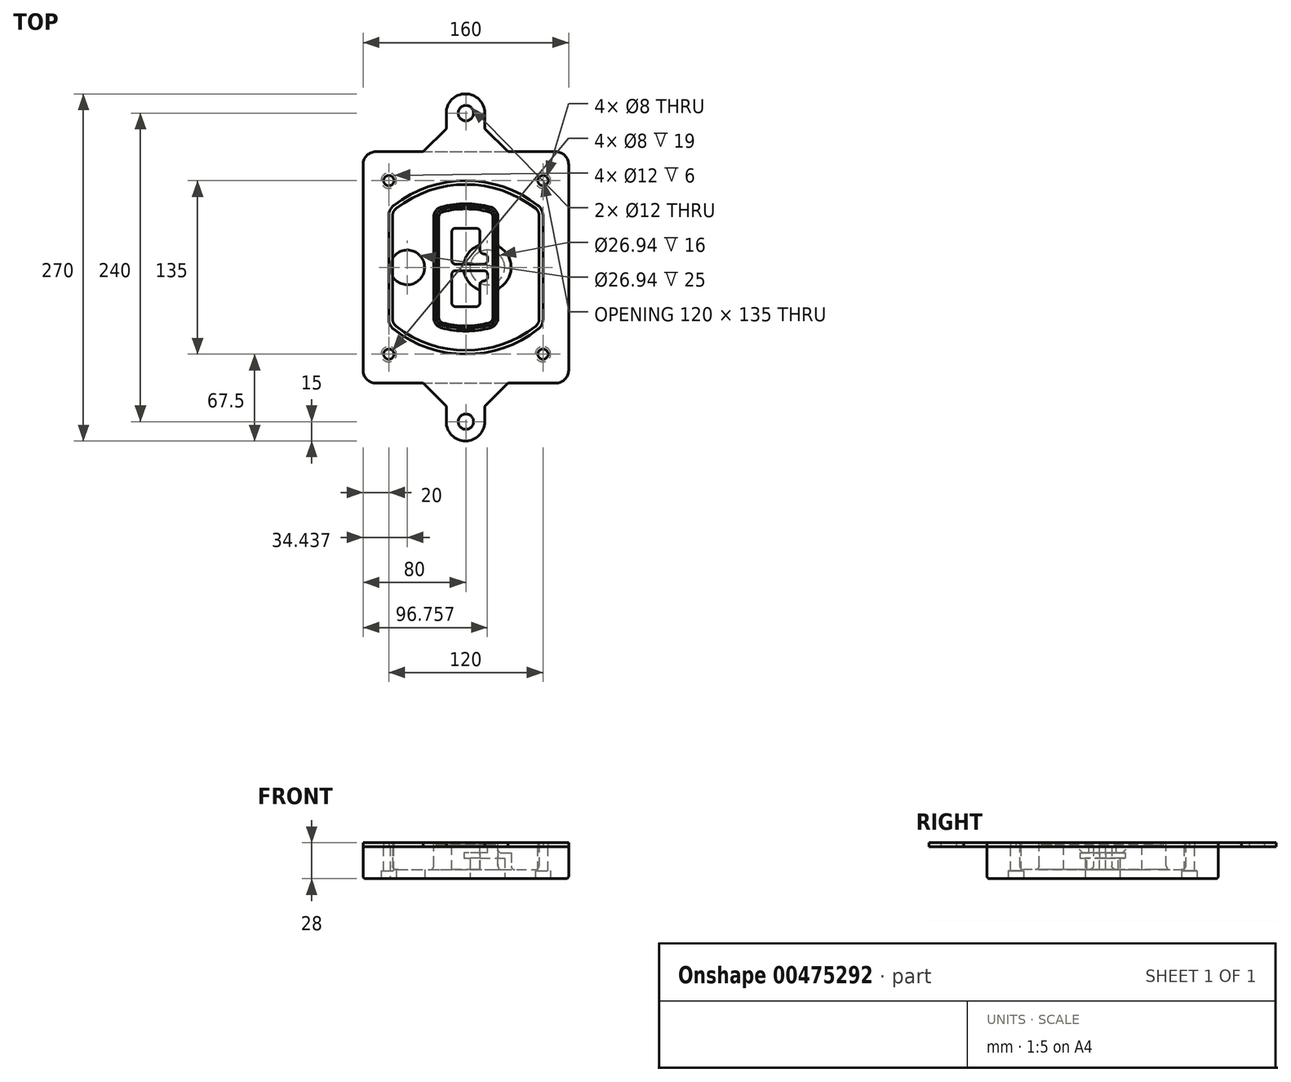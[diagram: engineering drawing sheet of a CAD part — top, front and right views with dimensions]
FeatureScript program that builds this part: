
annotation { "Feature Type Name" : "Feature", "Feature Type Description" : "" }
export const myFeature = defineFeature(function(context is Context, id is Id, definition is map)
    precondition{}
    {
        {
            var Q0;
            Q0=qCreatedBy(makeId("Top.planeOp"),FACE);
            var sketch = newSketch(context, id + "F0", { "sketchPlane" : qUnion([Q0])});
            skPoint(sketch, "E0.rect.middle", {"position": v(0, 0) * mm});
            skLineSegment(sketch, "E1.bottom", {"start": v(-70, -90) * mm, "end": v(70, -90) * mm});
            skLineSegment(sketch, "E1.top", {"start": v(-70, 90) * mm, "end": v(70, 90) * mm});
            skLineSegment(sketch, "E1.left", {"start": v(-80, -80) * mm, "end": v(-80, 80) * mm});
            skLineSegment(sketch, "E1.right", {"start": v(80, -80) * mm, "end": v(80, 80) * mm});
            skLineSegment(sketch, "E2", {"start": v(-80, 90) * mm, "end": v(80, -90) * mm, "construction": true});
            skLineSegment(sketch, "E3", {"start": v(80, 90) * mm, "end": v(-80, -90) * mm, "construction": true});
            skCircle(sketch, "E4", {"center": v(-60, 67.5) * mm, "radius": 4 * mm});
            skCircle(sketch, "E5", {"center": v(60, 67.5) * mm, "radius": 4 * mm});
            skCircle(sketch, "E6", {"center": v(60, -67.5) * mm, "radius": 4 * mm});
            skCircle(sketch, "E7", {"center": v(-60, -67.5) * mm, "radius": 4 * mm});
            skLineSegment(sketch, "E8", {"start": v(-60, 67.5) * mm, "end": v(60, 67.5) * mm, "construction": true});
            skLineSegment(sketch, "E9", {"start": v(60, 67.5) * mm, "end": v(60, -67.5) * mm, "construction": true});
            skLineSegment(sketch, "E10", {"start": v(60, -67.5) * mm, "end": v(-60, -67.5) * mm, "construction": true});
            skLineSegment(sketch, "E11", {"start": v(-60, -67.5) * mm, "end": v(-60, 67.5) * mm, "construction": true});
            skLineSegment(sketch, "E12", {"start": v(-60, 40.3) * mm, "end": v(-60, -40.3) * mm});
            skLineSegment(sketch, "E13", {"start": v(60, 40.3) * mm, "end": v(60, -40.3) * mm});
            skArc(sketch, "E14", {"start": v(56.15, 48.18) * mm, "mid": v(0, 67.5) * mm, "end": v(-56.15, 48.18) * mm});
            skArc(sketch, "E15", {"start": v(-56.15, -48.18) * mm, "mid": v(0, -67.5) * mm, "end": v(56.15, -48.18) * mm});
            skLineSegment(sketch, "E16", {"start": v(-60, 0) * mm, "end": v(60, 0) * mm, "construction": true});
            skPoint(sketch, "E17.visualSharp", {"position": v(-60, -45) * mm});
            skArc(sketch, "E17.filletArc", {"start": v(-60, -40.3) * mm, "mid": v(-58.99, -44.68) * mm, "end": v(-56.15, -48.18) * mm});
            skPoint(sketch, "E18.visualSharp", {"position": v(-60, 45) * mm});
            skArc(sketch, "E18.filletArc", {"start": v(-56.15, 48.18) * mm, "mid": v(-58.99, 44.68) * mm, "end": v(-60, 40.3) * mm});
            skPoint(sketch, "E19.visualSharp", {"position": v(60, 45) * mm});
            skArc(sketch, "E19.filletArc", {"start": v(60, 40.3) * mm, "mid": v(58.99, 44.68) * mm, "end": v(56.15, 48.18) * mm});
            skPoint(sketch, "E20.visualSharp", {"position": v(60, -45) * mm});
            skArc(sketch, "E20.filletArc", {"start": v(56.15, -48.18) * mm, "mid": v(58.99, -44.68) * mm, "end": v(60, -40.3) * mm});
            skPoint(sketch, "E21.visualSharp", {"position": v(-80, 90) * mm});
            skArc(sketch, "E21.filletArc", {"start": v(-70, 90) * mm, "mid": v(-77.07, 87.07) * mm, "end": v(-80, 80) * mm});
            skPoint(sketch, "E22.visualSharp", {"position": v(80, 90) * mm});
            skArc(sketch, "E22.filletArc", {"start": v(80, 80) * mm, "mid": v(77.07, 87.07) * mm, "end": v(70, 90) * mm});
            skPoint(sketch, "E23.visualSharp", {"position": v(80, -90) * mm});
            skArc(sketch, "E23.filletArc", {"start": v(70, -90) * mm, "mid": v(77.07, -87.07) * mm, "end": v(80, -80) * mm});
            skPoint(sketch, "E24.visualSharp", {"position": v(-80, -90) * mm});
            skArc(sketch, "E24.filletArc", {"start": v(-80, -80) * mm, "mid": v(-77.07, -87.07) * mm, "end": v(-70, -90) * mm});
            skArc(sketch, "E25.0", {"start": v(57, 40.3) * mm, "mid": v(56.3, 43.36) * mm, "end": v(54.3, 45.81) * mm});
            skLineSegment(sketch, "E25.1", {"start": v(57, 40.3) * mm, "end": v(57, -40.3) * mm});
            skArc(sketch, "E25.2", {"start": v(54.3, -45.81) * mm, "mid": v(56.3, -43.36) * mm, "end": v(57, -40.3) * mm});
            skArc(sketch, "E25.3", {"start": v(-54.3, -45.81) * mm, "mid": v(0, -64.5) * mm, "end": v(54.3, -45.81) * mm});
            skArc(sketch, "E25.4", {"start": v(-57, -40.3) * mm, "mid": v(-56.3, -43.36) * mm, "end": v(-54.3, -45.81) * mm});
            skArc(sketch, "E25.5", {"start": v(54.3, 45.81) * mm, "mid": v(0, 64.5) * mm, "end": v(-54.3, 45.81) * mm});
            skLineSegment(sketch, "E25.6", {"start": v(-57, 40.3) * mm, "end": v(-57, -40.3) * mm});
            skArc(sketch, "E25.7", {"start": v(-54.3, 45.81) * mm, "mid": v(-56.3, 43.36) * mm, "end": v(-57, 40.3) * mm});
            skArc(sketch, "E26.0", {"start": v(-58.62, 51.33) * mm, "mid": v(-62.58, 46.43) * mm, "end": v(-64, 40.3) * mm});
            skArc(sketch, "E26.1", {"start": v(58.62, 51.33) * mm, "mid": v(0, 71.5) * mm, "end": v(-58.62, 51.33) * mm});
            skArc(sketch, "E26.2", {"start": v(64, 40.3) * mm, "mid": v(62.58, 46.43) * mm, "end": v(58.62, 51.33) * mm});
            skLineSegment(sketch, "E26.3", {"start": v(64, 40.3) * mm, "end": v(64, -40.3) * mm});
            skArc(sketch, "E26.4", {"start": v(58.62, -51.33) * mm, "mid": v(62.58, -46.43) * mm, "end": v(64, -40.3) * mm});
            skLineSegment(sketch, "E26.5", {"start": v(-64, 40.3) * mm, "end": v(-64, -40.3) * mm});
            skArc(sketch, "E26.6", {"start": v(-58.62, -51.33) * mm, "mid": v(0, -71.5) * mm, "end": v(58.62, -51.33) * mm});
            skArc(sketch, "E26.7", {"start": v(-64, -40.3) * mm, "mid": v(-62.58, -46.43) * mm, "end": v(-58.62, -51.33) * mm});
            skSolve(sketch);
        }
        {
            var Q0;
            Q0=makeQuery(id+"F0.imprint","IMPRINT",FACE,{"disambiguationData":[TD([[makeQuery(id+"F0.imprint","IMPRINT",EDGE,{"derivedFrom":sQuery(id+"F0.wireOp",EDGE,"E1.bottom")}),1.0]])]});
            var Q1;
            Q1=makeQuery(id+"F0.imprint","IMPRINT",FACE,{"disambiguationData":[TD([[makeQuery(id+"F0.imprint","IMPRINT",EDGE,{"derivedFrom":sQuery(id+"F0.wireOp",EDGE,"E12")}),1.0]])]});
            var Q2;
            Q2=makeQuery(id+"F0.imprint","IMPRINT",FACE,{"disambiguationData":[TD([[makeQuery(id+"F0.imprint","IMPRINT",EDGE,{"derivedFrom":sQuery(id+"F0.wireOp",EDGE,"E25.0")}),1.0]])]});
            var Q3;
            Q3=makeQuery(id+"F0.imprint","IMPRINT",FACE,{"disambiguationData":[TD([[makeQuery(id+"F0.imprint","IMPRINT",EDGE,{"derivedFrom":sQuery(id+"F0.wireOp",EDGE,"E12")}),-1.0]])]});
            extrude(context, id + "F1", {"entities" : qUnion([Q0, Q1, Q2, Q3]), "oppositeDirection" : true, "depth" : 25 * mm});
        }
        {
            var Q0;
            Q0=makeQuery(id+"F0.imprint","IMPRINT",FACE,{"disambiguationData":[TD([[makeQuery(id+"F0.imprint","IMPRINT",EDGE,{"derivedFrom":sQuery(id+"F0.wireOp",EDGE,"E12")}),1.0]])]});
            extrude(context, id + "F2", {"entities" : qUnion([Q0]), "operationType" : NewBodyOperationType.ADD, "depth" : 3 * mm});
        }
        {
            var Q0;
            Q0=makeQuery(id+"F0.imprint","IMPRINT",FACE,{"disambiguationData":[TD([[makeQuery(id+"F0.imprint","IMPRINT",EDGE,{"derivedFrom":sQuery(id+"F0.wireOp",EDGE,"E25.0")}),1.0]])]});
            extrude(context, id + "F3", {"entities" : qUnion([Q0]), "operationType" : NewBodyOperationType.REMOVE, "oppositeDirection" : true, "depth" : 18 * mm});
        }
        {
            var Q0;
            Q0=makeQuery(id+"F2.opExtrude","CAP_FACE",FACE,{"disambiguationData":[OSD([sQuery(id+"F0.wireOp",EDGE,"E12"),sQuery(id+"F0.wireOp",EDGE,"E13"),sQuery(id+"F0.wireOp",EDGE,"E14"),sQuery(id+"F0.wireOp",EDGE,"E15"),sQuery(id+"F0.wireOp",EDGE,"E17.filletArc"),sQuery(id+"F0.wireOp",EDGE,"E18.filletArc"),sQuery(id+"F0.wireOp",EDGE,"E19.filletArc"),sQuery(id+"F0.wireOp",EDGE,"E20.filletArc"),sQuery(id+"F0.wireOp",EDGE,"E25.0"),sQuery(id+"F0.wireOp",EDGE,"E25.1"),sQuery(id+"F0.wireOp",EDGE,"E25.2"),sQuery(id+"F0.wireOp",EDGE,"E25.3"),sQuery(id+"F0.wireOp",EDGE,"E25.4"),sQuery(id+"F0.wireOp",EDGE,"E25.5"),sQuery(id+"F0.wireOp",EDGE,"E25.6"),sQuery(id+"F0.wireOp",EDGE,"E25.7")])],"isStart":false});
            var sketch = newSketch(context, id + "F4", { "sketchPlane" : qUnion([Q0])});
            skArc(sketch, "E27.0", {"start": v(-19.08, -46.97) * mm, "mid": v(0, -49.5) * mm, "end": v(19.08, -46.97) * mm});
            skArc(sketch, "E28.0", {"start": v(19.08, 46.97) * mm, "mid": v(0, 49.5) * mm, "end": v(-19.08, 46.97) * mm});
            skLineSegment(sketch, "E29", {"start": v(-25, 39.25) * mm, "end": v(-25, -39.25) * mm});
            skLineSegment(sketch, "E30", {"start": v(25, 39.25) * mm, "end": v(25, -39.25) * mm});
            skLineSegment(sketch, "E31", {"start": v(-25, 45.1) * mm, "end": v(25, 45.1) * mm, "construction": true});
            skLineSegment(sketch, "E32", {"start": v(-25, -45.1) * mm, "end": v(25, -45.1) * mm, "construction": true});
            skPoint(sketch, "E33.visualSharp", {"position": v(-25, 45.1) * mm});
            skArc(sketch, "E33.filletArc", {"start": v(-19.08, 46.97) * mm, "mid": v(-23.35, 44.11) * mm, "end": v(-25, 39.25) * mm});
            skPoint(sketch, "E34.visualSharp", {"position": v(25, 45.1) * mm});
            skArc(sketch, "E34.filletArc", {"start": v(25, 39.25) * mm, "mid": v(23.35, 44.11) * mm, "end": v(19.08, 46.97) * mm});
            skPoint(sketch, "E35.visualSharp", {"position": v(25, -45.1) * mm});
            skArc(sketch, "E35.filletArc", {"start": v(19.08, -46.97) * mm, "mid": v(23.35, -44.11) * mm, "end": v(25, -39.25) * mm});
            skPoint(sketch, "E36.visualSharp", {"position": v(-25, -45.1) * mm});
            skArc(sketch, "E36.filletArc", {"start": v(-25, -39.25) * mm, "mid": v(-23.35, -44.11) * mm, "end": v(-19.08, -46.97) * mm});
            skArc(sketch, "E37.0", {"start": v(54.3, 45.81) * mm, "mid": v(0, 64.5) * mm, "end": v(-54.3, 45.81) * mm});
            skArc(sketch, "E37.1", {"start": v(-54.3, 45.81) * mm, "mid": v(-56.3, 43.36) * mm, "end": v(-57, 40.3) * mm});
            skLineSegment(sketch, "E37.2", {"start": v(-57, 40.3) * mm, "end": v(-57, -40.3) * mm});
            skArc(sketch, "E37.3", {"start": v(-57, -40.3) * mm, "mid": v(-56.3, -43.36) * mm, "end": v(-54.3, -45.81) * mm});
            skArc(sketch, "E37.4", {"start": v(-54.3, -45.81) * mm, "mid": v(0, -64.5) * mm, "end": v(54.3, -45.81) * mm});
            skArc(sketch, "E37.5", {"start": v(54.3, -45.81) * mm, "mid": v(56.3, -43.36) * mm, "end": v(57, -40.3) * mm});
            skLineSegment(sketch, "E37.6", {"start": v(57, 40.3) * mm, "end": v(57, -40.3) * mm});
            skArc(sketch, "E37.7", {"start": v(57, 40.3) * mm, "mid": v(56.3, 43.36) * mm, "end": v(54.3, 45.81) * mm});
            skLineSegment(sketch, "E38.0", {"start": v(23, 39.25) * mm, "end": v(23, -39.25) * mm});
            skArc(sketch, "E38.1", {"start": v(18.56, -45.04) * mm, "mid": v(21.76, -42.9) * mm, "end": v(23, -39.25) * mm});
            skArc(sketch, "E38.2", {"start": v(-18.56, -45.04) * mm, "mid": v(0, -47.5) * mm, "end": v(18.56, -45.04) * mm});
            skArc(sketch, "E38.3", {"start": v(-23, -39.25) * mm, "mid": v(-21.76, -42.9) * mm, "end": v(-18.56, -45.04) * mm});
            skLineSegment(sketch, "E38.4", {"start": v(-23, 39.25) * mm, "end": v(-23, -39.25) * mm});
            skArc(sketch, "E38.5", {"start": v(23, 39.25) * mm, "mid": v(21.76, 42.9) * mm, "end": v(18.56, 45.04) * mm});
            skArc(sketch, "E38.6", {"start": v(-18.56, 45.04) * mm, "mid": v(-21.76, 42.9) * mm, "end": v(-23, 39.25) * mm});
            skArc(sketch, "E38.7", {"start": v(18.56, 45.04) * mm, "mid": v(0, 47.5) * mm, "end": v(-18.56, 45.04) * mm});
            skArc(sketch, "E39.0", {"start": v(21, 39.25) * mm, "mid": v(20.18, 41.68) * mm, "end": v(18.04, 43.1) * mm});
            skLineSegment(sketch, "E39.1", {"start": v(21, 39.25) * mm, "end": v(21, -39.25) * mm});
            skArc(sketch, "E39.2", {"start": v(18.04, -43.1) * mm, "mid": v(20.18, -41.68) * mm, "end": v(21, -39.25) * mm});
            skArc(sketch, "E39.3", {"start": v(-18.04, -43.1) * mm, "mid": v(0, -45.5) * mm, "end": v(18.04, -43.1) * mm});
            skArc(sketch, "E39.4", {"start": v(-21, -39.25) * mm, "mid": v(-20.18, -41.68) * mm, "end": v(-18.04, -43.1) * mm});
            skArc(sketch, "E39.5", {"start": v(18.04, 43.1) * mm, "mid": v(0, 45.5) * mm, "end": v(-18.04, 43.1) * mm});
            skLineSegment(sketch, "E39.6", {"start": v(-21, 39.25) * mm, "end": v(-21, -39.25) * mm});
            skArc(sketch, "E39.7", {"start": v(-18.04, 43.1) * mm, "mid": v(-20.18, 41.68) * mm, "end": v(-21, 39.25) * mm});
            skLineSegment(sketch, "E40", {"start": v(-25, 0) * mm, "end": v(25, 0) * mm, "construction": true});
            skLineSegment(sketch, "E41", {"start": v(-11, 5.5) * mm, "end": v(-11, 27.5) * mm});
            skLineSegment(sketch, "E42", {"start": v(-8, 30.5) * mm, "end": v(8, 30.5) * mm});
            skLineSegment(sketch, "E43", {"start": v(11, 27.5) * mm, "end": v(11, 13.5) * mm});
            skLineSegment(sketch, "E44", {"start": v(14, 10.5) * mm, "end": v(14, 10.5) * mm});
            skLineSegment(sketch, "E45", {"start": v(17, 7.5) * mm, "end": v(17, 5.5) * mm});
            skLineSegment(sketch, "E46", {"start": v(14, 2.5) * mm, "end": v(-8, 2.5) * mm});
            skPoint(sketch, "E47.visualSharp", {"position": v(-11, 30.5) * mm});
            skArc(sketch, "E47.filletArc", {"start": v(-8, 30.5) * mm, "mid": v(-10.12, 29.62) * mm, "end": v(-11, 27.5) * mm});
            skPoint(sketch, "E48.visualSharp", {"position": v(11, 30.5) * mm});
            skArc(sketch, "E48.filletArc", {"start": v(11, 27.5) * mm, "mid": v(10.12, 29.62) * mm, "end": v(8, 30.5) * mm});
            skPoint(sketch, "E49.visualSharp", {"position": v(11, 10.5) * mm});
            skArc(sketch, "E49.filletArc", {"start": v(11, 13.5) * mm, "mid": v(11.88, 11.38) * mm, "end": v(14, 10.5) * mm});
            skPoint(sketch, "E50.visualSharp", {"position": v(17, 10.5) * mm});
            skArc(sketch, "E50.filletArc", {"start": v(17, 7.5) * mm, "mid": v(16.12, 9.62) * mm, "end": v(14, 10.5) * mm});
            skPoint(sketch, "E51.visualSharp", {"position": v(17, 2.5) * mm});
            skArc(sketch, "E51.filletArc", {"start": v(14, 2.5) * mm, "mid": v(16.12, 3.38) * mm, "end": v(17, 5.5) * mm});
            skPoint(sketch, "E52.visualSharp", {"position": v(-11, 2.5) * mm});
            skArc(sketch, "E52.filletArc", {"start": v(-11, 5.5) * mm, "mid": v(-10.12, 3.38) * mm, "end": v(-8, 2.5) * mm});
            skLineSegment(sketch, "E53.0.MirrorCS", {"start": v(14, -2.5) * mm, "end": v(-8, -2.5) * mm});
            skArc(sketch, "E54.0.MirrorCS", {"start": v(-11, -5.5) * mm, "mid": v(-10.12, -3.38) * mm, "end": v(-8, -2.5) * mm});
            skLineSegment(sketch, "E55.0.MirrorCS", {"start": v(-11, -5.5) * mm, "end": v(-11, -27.5) * mm});
            skArc(sketch, "E56.0.MirrorCS", {"start": v(-8, -30.5) * mm, "mid": v(-10.12, -29.62) * mm, "end": v(-11, -27.5) * mm});
            skLineSegment(sketch, "E57.0.MirrorCS", {"start": v(-8, -30.5) * mm, "end": v(8, -30.5) * mm});
            skArc(sketch, "E58.0.MirrorCS", {"start": v(11, -27.5) * mm, "mid": v(10.12, -29.62) * mm, "end": v(8, -30.5) * mm});
            skLineSegment(sketch, "E59.0.MirrorCS", {"start": v(11, -27.5) * mm, "end": v(11, -13.5) * mm});
            skArc(sketch, "E60.0.MirrorCS", {"start": v(11, -13.5) * mm, "mid": v(11.88, -11.38) * mm, "end": v(14, -10.5) * mm});
            skArc(sketch, "E61.0.MirrorCS", {"start": v(17, -7.5) * mm, "mid": v(16.12, -9.62) * mm, "end": v(14, -10.5) * mm});
            skLineSegment(sketch, "E62.0.MirrorCS", {"start": v(17, -7.5) * mm, "end": v(17, -5.5) * mm});
            skArc(sketch, "E63.0.MirrorCS", {"start": v(14, -2.5) * mm, "mid": v(16.12, -3.38) * mm, "end": v(17, -5.5) * mm});
            skSolve(sketch);
        }
        {
            var Q0;
            Q0=makeQuery(id+"F4.imprint","IMPRINT",FACE,{"disambiguationData":[TD([[makeQuery(id+"F4.imprint","IMPRINT",EDGE,{"derivedFrom":sQuery(id+"F4.wireOp",EDGE,"E27.0")}),1.0]])]});
            var Q1;
            Q1=makeQuery(id+"F4.imprint","IMPRINT",FACE,{"disambiguationData":[TD([[makeQuery(id+"F4.imprint","IMPRINT",EDGE,{"derivedFrom":sQuery(id+"F4.wireOp",EDGE,"E38.0")}),-1.0]])]});
            var Q2;
            Q2=makeQuery(id+"F4.imprint","IMPRINT",FACE,{"disambiguationData":[TD([[makeQuery(id+"F4.imprint","IMPRINT",EDGE,{"derivedFrom":sQuery(id+"F4.wireOp",EDGE,"E39.0")}),1.0]])]});
            extrude(context, id + "F5", {"entities" : qUnion([Q0, Q1, Q2]), "operationType" : NewBodyOperationType.ADD, "endBound" : BoundingType.UP_TO_NEXT, "oppositeDirection" : true, "depth" : 25 * mm});
        }
        {
            var Q0;
            Q0=makeQuery(id+"F4.imprint","IMPRINT",FACE,{"disambiguationData":[TD([[makeQuery(id+"F4.imprint","IMPRINT",EDGE,{"derivedFrom":sQuery(id+"F4.wireOp",EDGE,"E38.0")}),-1.0]])]});
            extrude(context, id + "F6", {"entities" : qUnion([Q0]), "operationType" : NewBodyOperationType.REMOVE, "oppositeDirection" : true, "depth" : 2 * mm});
        }
        {
            var Q0;
            Q0=makeQuery(id+"F1.opExtrude","CAP_FACE",FACE,{"disambiguationData":[OSD([sQuery(id+"F0.wireOp",EDGE,"E1.bottom"),sQuery(id+"F0.wireOp",EDGE,"E1.top"),sQuery(id+"F0.wireOp",EDGE,"E1.left"),sQuery(id+"F0.wireOp",EDGE,"E1.right"),sQuery(id+"F0.wireOp",EDGE,"E4"),sQuery(id+"F0.wireOp",EDGE,"E5"),sQuery(id+"F0.wireOp",EDGE,"E6"),sQuery(id+"F0.wireOp",EDGE,"E7"),sQuery(id+"F0.wireOp",EDGE,"E21.filletArc"),sQuery(id+"F0.wireOp",EDGE,"E22.filletArc"),sQuery(id+"F0.wireOp",EDGE,"E23.filletArc"),sQuery(id+"F0.wireOp",EDGE,"E24.filletArc")])],"isStart":false});
            var sketch = newSketch(context, id + "F7", { "sketchPlane" : qUnion([Q0])});
            skCircle(sketch, "E64", {"center": v(16.76, 0) * mm, "radius": 13.47 * mm});
            skCircle(sketch, "E65", {"center": v(-45.56, 0) * mm, "radius": 13.47 * mm});
            skLineSegment(sketch, "E66", {"start": v(80, 0) * mm, "end": v(-80, 0) * mm});
            skCircle(sketch, "E67", {"center": v(16.76, 0) * mm, "radius": 18.47 * mm});
            skCircle(sketch, "E68", {"center": v(60, -67.5) * mm, "radius": 6 * mm});
            skCircle(sketch, "E69", {"center": v(-60, -67.5) * mm, "radius": 6 * mm});
            skCircle(sketch, "E70", {"center": v(-60, 67.5) * mm, "radius": 6 * mm});
            skCircle(sketch, "E71", {"center": v(60, 67.5) * mm, "radius": 6 * mm});
            skSolve(sketch);
        }
        {
            var Q0;
            {var subQ1=sQuery(id+"F7.wireOp",EDGE,"E66");var subQ4=sQuery(id+"F7.wireOp",EDGE,"E64");var subQ6=makeQuery(id+"F7.imprint","INTERSECT",VERTEX,{"disambiguationData":[OD(0.0)],"derivedFrom":[subQ4,subQ1]});Q0=makeQuery(id+"F7.imprint","IMPRINT",FACE,{"disambiguationData":[TD([[makeQuery(id+"F7.imprint","IMPRINT",EDGE,{"disambiguationData":[TD([[subQ6,-1.0]])],"derivedFrom":subQ4}),-1.0]])]});}
            var Q1;
            {var subQ0=sQuery(id+"F7.wireOp",EDGE,"E66");var subQ1=sQuery(id+"F7.wireOp",EDGE,"E64");var subQ3=makeQuery(id+"F7.imprint","INTERSECT",VERTEX,{"disambiguationData":[OD(0.0)],"derivedFrom":[subQ1,subQ0]});Q1=makeQuery(id+"F7.imprint","IMPRINT",FACE,{"disambiguationData":[TD([[makeQuery(id+"F7.imprint","IMPRINT",EDGE,{"disambiguationData":[TD([[subQ3,-1.0]])],"derivedFrom":subQ1}),1.0]])]});}
            var Q2;
            {var subQ0=sQuery(id+"F7.wireOp",EDGE,"E66");var subQ1=sQuery(id+"F7.wireOp",EDGE,"E64");var subQ3=makeQuery(id+"F7.imprint","INTERSECT",VERTEX,{"disambiguationData":[OD(0.0)],"derivedFrom":[subQ1,subQ0]});Q2=makeQuery(id+"F7.imprint","IMPRINT",FACE,{"disambiguationData":[TD([[makeQuery(id+"F7.imprint","IMPRINT",EDGE,{"disambiguationData":[TD([[subQ3,1.0]])],"derivedFrom":subQ1}),1.0]])]});}
            var Q3;
            {var subQ1=sQuery(id+"F7.wireOp",EDGE,"E66");var subQ4=sQuery(id+"F7.wireOp",EDGE,"E64");var subQ6=makeQuery(id+"F7.imprint","INTERSECT",VERTEX,{"disambiguationData":[OD(0.0)],"derivedFrom":[subQ4,subQ1]});Q3=makeQuery(id+"F7.imprint","IMPRINT",FACE,{"disambiguationData":[TD([[makeQuery(id+"F7.imprint","IMPRINT",EDGE,{"disambiguationData":[TD([[subQ6,1.0]])],"derivedFrom":subQ4}),-1.0]])]});}
            extrude(context, id + "F8", {"entities" : qUnion([Q0, Q1, Q2, Q3]), "operationType" : NewBodyOperationType.ADD, "oppositeDirection" : true, "depth" : 20 * mm});
        }
        {
            var Q0;
            {var subQ0=sQuery(id+"F7.wireOp",EDGE,"E66");var subQ1=sQuery(id+"F7.wireOp",EDGE,"E64");var subQ3=makeQuery(id+"F7.imprint","INTERSECT",VERTEX,{"disambiguationData":[OD(0.0)],"derivedFrom":[subQ1,subQ0]});Q0=makeQuery(id+"F7.imprint","IMPRINT",FACE,{"disambiguationData":[TD([[makeQuery(id+"F7.imprint","IMPRINT",EDGE,{"disambiguationData":[TD([[subQ3,-1.0]])],"derivedFrom":subQ1}),1.0]])]});}
            var Q1;
            {var subQ0=sQuery(id+"F7.wireOp",EDGE,"E66");var subQ1=sQuery(id+"F7.wireOp",EDGE,"E64");var subQ3=makeQuery(id+"F7.imprint","INTERSECT",VERTEX,{"disambiguationData":[OD(0.0)],"derivedFrom":[subQ1,subQ0]});Q1=makeQuery(id+"F7.imprint","IMPRINT",FACE,{"disambiguationData":[TD([[makeQuery(id+"F7.imprint","IMPRINT",EDGE,{"disambiguationData":[TD([[subQ3,1.0]])],"derivedFrom":subQ1}),1.0]])]});}
            extrude(context, id + "F9", {"entities" : qUnion([Q0, Q1]), "operationType" : NewBodyOperationType.REMOVE, "oppositeDirection" : true, "depth" : 16 * mm});
        }
        {
            var Q0;
            {var subQ0=sQuery(id+"F7.wireOp",EDGE,"E66");var subQ1=sQuery(id+"F7.wireOp",EDGE,"E65");var subQ3=makeQuery(id+"F7.imprint","INTERSECT",VERTEX,{"disambiguationData":[OD(0.0)],"derivedFrom":[subQ1,subQ0]});Q0=makeQuery(id+"F7.imprint","IMPRINT",FACE,{"disambiguationData":[TD([[makeQuery(id+"F7.imprint","IMPRINT",EDGE,{"disambiguationData":[TD([[subQ3,-1.0]])],"derivedFrom":subQ1}),1.0]])]});}
            var Q1;
            {var subQ0=sQuery(id+"F7.wireOp",EDGE,"E66");var subQ1=sQuery(id+"F7.wireOp",EDGE,"E65");var subQ3=makeQuery(id+"F7.imprint","INTERSECT",VERTEX,{"disambiguationData":[OD(0.0)],"derivedFrom":[subQ1,subQ0]});Q1=makeQuery(id+"F7.imprint","IMPRINT",FACE,{"disambiguationData":[TD([[makeQuery(id+"F7.imprint","IMPRINT",EDGE,{"disambiguationData":[TD([[subQ3,1.0]])],"derivedFrom":subQ1}),1.0]])]});}
            extrude(context, id + "F10", {"entities" : qUnion([Q0, Q1]), "operationType" : NewBodyOperationType.REMOVE, "oppositeDirection" : true, "depth" : 25 * mm});
        }
        {
            var Q0;
            Q0=makeQuery(id+"F7.imprint","IMPRINT",FACE,{"disambiguationData":[TD([[makeQuery(id+"F7.imprint","IMPRINT",EDGE,{"derivedFrom":sQuery(id+"F7.wireOp",EDGE,"E68")}),1.0]])]});
            var Q1;
            Q1=makeQuery(id+"F7.imprint","IMPRINT",FACE,{"disambiguationData":[TD([[makeQuery(id+"F7.imprint","IMPRINT",EDGE,{"derivedFrom":makeQuery(id+"F1.opExtrude","CAP_EDGE",EDGE,{"disambiguationData":[OSD([sQuery(id+"F0.wireOp",EDGE,"E5")])],"isStart":false})}),-1.0]])]});
            var Q2;
            Q2=makeQuery(id+"F7.imprint","IMPRINT",FACE,{"disambiguationData":[TD([[makeQuery(id+"F7.imprint","IMPRINT",EDGE,{"derivedFrom":sQuery(id+"F7.wireOp",EDGE,"E69")}),1.0]])]});
            var Q3;
            Q3=makeQuery(id+"F7.imprint","IMPRINT",FACE,{"disambiguationData":[TD([[makeQuery(id+"F7.imprint","IMPRINT",EDGE,{"derivedFrom":makeQuery(id+"F1.opExtrude","CAP_EDGE",EDGE,{"disambiguationData":[OSD([sQuery(id+"F0.wireOp",EDGE,"E4")])],"isStart":false})}),-1.0]])]});
            var Q4;
            Q4=makeQuery(id+"F7.imprint","IMPRINT",FACE,{"disambiguationData":[TD([[makeQuery(id+"F7.imprint","IMPRINT",EDGE,{"derivedFrom":sQuery(id+"F7.wireOp",EDGE,"E70")}),1.0]])]});
            var Q5;
            Q5=makeQuery(id+"F7.imprint","IMPRINT",FACE,{"disambiguationData":[TD([[makeQuery(id+"F7.imprint","IMPRINT",EDGE,{"derivedFrom":makeQuery(id+"F1.opExtrude","CAP_EDGE",EDGE,{"disambiguationData":[OSD([sQuery(id+"F0.wireOp",EDGE,"E7")])],"isStart":false})}),-1.0]])]});
            var Q6;
            Q6=makeQuery(id+"F7.imprint","IMPRINT",FACE,{"disambiguationData":[TD([[makeQuery(id+"F7.imprint","IMPRINT",EDGE,{"derivedFrom":sQuery(id+"F7.wireOp",EDGE,"E71")}),1.0]])]});
            var Q7;
            Q7=makeQuery(id+"F7.imprint","IMPRINT",FACE,{"disambiguationData":[TD([[makeQuery(id+"F7.imprint","IMPRINT",EDGE,{"derivedFrom":makeQuery(id+"F1.opExtrude","CAP_EDGE",EDGE,{"disambiguationData":[OSD([sQuery(id+"F0.wireOp",EDGE,"E6")])],"isStart":false})}),-1.0]])]});
            extrude(context, id + "F11", {"entities" : qUnion([Q0, Q1, Q2, Q3, Q4, Q5, Q6, Q7]), "operationType" : NewBodyOperationType.REMOVE, "oppositeDirection" : true, "depth" : 6 * mm});
        }
        {
            var Q0;
            Q0=makeQuery(id+"F9.boolean.opBoolean","COPY",FACE,{"derivedFrom":makeQuery(id+"F9.opExtrude","CAP_FACE",FACE,{"disambiguationData":[OSD([sQuery(id+"F7.wireOp",EDGE,"E64")])],"isStart":false})});
            var sketch = newSketch(context, id + "F12", { "sketchPlane" : qUnion([Q0])});
            skArc(sketch, "E72.0", {"start": v(11, 17.55) * mm, "mid": v(2.57, 11.82) * mm, "end": v(-1.54, 2.5) * mm});
            skArc(sketch, "E72.1", {"start": v(-1.54, -2.5) * mm, "mid": v(2.57, -11.82) * mm, "end": v(11, -17.55) * mm});
            skLineSegment(sketch, "E73", {"start": v(-1.54, -2.5) * mm, "end": v(14, -2.5) * mm});
            skLineSegment(sketch, "E74.0", {"start": v(14, 2.5) * mm, "end": v(-1.54, 2.5) * mm});
            skArc(sketch, "E74.1", {"start": v(14, 2.5) * mm, "mid": v(16.12, 3.38) * mm, "end": v(17, 5.5) * mm});
            skLineSegment(sketch, "E74.2", {"start": v(17, 7.5) * mm, "end": v(17, 5.5) * mm});
            skArc(sketch, "E74.3", {"start": v(17, 7.5) * mm, "mid": v(16.12, 9.62) * mm, "end": v(14, 10.5) * mm});
            skArc(sketch, "E74.4", {"start": v(11, 13.5) * mm, "mid": v(11.88, 11.38) * mm, "end": v(14, 10.5) * mm});
            skLineSegment(sketch, "E74.5", {"start": v(11, 17.55) * mm, "end": v(11, 13.5) * mm});
            skLineSegment(sketch, "E74.7", {"start": v(14, -2.5) * mm, "end": v(-1.54, -2.5) * mm});
            skArc(sketch, "E74.8", {"start": v(14, -2.5) * mm, "mid": v(16.12, -3.38) * mm, "end": v(17, -5.5) * mm});
            skLineSegment(sketch, "E74.9", {"start": v(17, -7.5) * mm, "end": v(17, -5.5) * mm});
            skArc(sketch, "E74.10", {"start": v(17, -7.5) * mm, "mid": v(16.12, -9.62) * mm, "end": v(14, -10.5) * mm});
            skArc(sketch, "E74.11", {"start": v(11, -13.5) * mm, "mid": v(11.88, -11.38) * mm, "end": v(14, -10.5) * mm});
            skLineSegment(sketch, "E74.12", {"start": v(11, -17.55) * mm, "end": v(11, -13.5) * mm});
            skPoint(sketch, "E75.orphan", {"position": v(11, -27.5) * mm});
            skPoint(sketch, "E76.orphan", {"position": v(-8, -2.5) * mm});
            skPoint(sketch, "E77.orphan", {"position": v(-8, 2.5) * mm});
            skPoint(sketch, "E78.orphan", {"position": v(11, 27.5) * mm});
            skSolve(sketch);
        }
        {
            var Q0;
            {var subQ7=sQuery(id+"F12.wireOp",EDGE,"E72.0");var subQ14=sQuery(id+"F12.wireOp",EDGE,"E72.1");var subQ16=sQuery(id+"F12.wireOp",EDGE,"E74.1");var subQ18=sQuery(id+"F12.wireOp",EDGE,"E74.8");Q0=qUnion([makeQuery(id+"F12.imprint","IMPRINT",FACE,{"disambiguationData":[TD([[makeQuery(id+"F12.imprint","IMPRINT",EDGE,{"derivedFrom":subQ7}),1.0]])]}),makeQuery(id+"F12.imprint","IMPRINT",FACE,{"disambiguationData":[TD([[makeQuery(id+"F12.imprint","IMPRINT",EDGE,{"derivedFrom":subQ14}),1.0]])]}),makeQuery(id+"F12.imprint","IMPRINT",FACE,{"disambiguationData":[TD([[makeQuery(id+"F12.imprint","IMPRINT",EDGE,{"derivedFrom":subQ16}),1.0]])]}),makeQuery(id+"F12.imprint","IMPRINT",FACE,{"disambiguationData":[TD([[makeQuery(id+"F12.imprint","IMPRINT",EDGE,{"derivedFrom":subQ18}),-1.0]])]})]);}
            var Q1;
            Q1=makeQuery(id+"F5.boolean.opBoolean","SPLIT",FACE,{"disambiguationData":[TD([makeQuery(id+"F5.opExtrude","SWEPT_FACE",FACE,{"disambiguationData":[OSD([sQuery(id+"F4.wireOp",EDGE,"E41")])]})])],"derivedFrom":makeQuery(id+"F3.boolean.opBoolean","COPY",FACE,{"derivedFrom":makeQuery(id+"F3.opExtrude","CAP_FACE",FACE,{"disambiguationData":[OSD([sQuery(id+"F0.wireOp",EDGE,"E25.0"),sQuery(id+"F0.wireOp",EDGE,"E25.1"),sQuery(id+"F0.wireOp",EDGE,"E25.2"),sQuery(id+"F0.wireOp",EDGE,"E25.3"),sQuery(id+"F0.wireOp",EDGE,"E25.4"),sQuery(id+"F0.wireOp",EDGE,"E25.5"),sQuery(id+"F0.wireOp",EDGE,"E25.6"),sQuery(id+"F0.wireOp",EDGE,"E25.7")])],"isStart":false})})});
            extrude(context, id + "F13", {"entities" : qUnion([Q0]), "operationType" : NewBodyOperationType.REMOVE, "endBound" : BoundingType.UP_TO_SURFACE, "endBoundEntityFace" : qUnion([Q1]), "depth" : 25 * mm});
        }
        {
            var Q0;
            Q0=makeQuery(id+"F3.boolean.opBoolean","COPY",EDGE,{"derivedFrom":makeQuery(id+"F3.opExtrude","CAP_EDGE",EDGE,{"disambiguationData":[OSD([sQuery(id+"F0.wireOp",EDGE,"E25.6")])],"isStart":false})});
            var Q1;
            Q1=makeQuery(id+"F8.boolean.opBoolean","INTERSECT",EDGE,{"derivedFrom":[makeQuery(id+"F5.opExtrude","SWEPT_FACE",FACE,{"disambiguationData":[OSD([sQuery(id+"F4.wireOp",EDGE,"E30")])]}),makeQuery(id+"F8.opExtrude","CAP_FACE",FACE,{"disambiguationData":[OSD([sQuery(id+"F7.wireOp",EDGE,"E67")])],"isStart":false})]});
            var Q2;
            Q2=makeQuery(id+"F8.boolean.opBoolean","INTERSECT",EDGE,{"disambiguationData":[OD(1.0)],"derivedFrom":[makeQuery(id+"F5.opExtrude","SWEPT_FACE",FACE,{"disambiguationData":[OSD([sQuery(id+"F4.wireOp",EDGE,"E30")])]}),makeQuery(id+"F8.opExtrude","SWEPT_FACE",FACE,{"disambiguationData":[OSD([sQuery(id+"F7.wireOp",EDGE,"E67")])]})]});
            var Q3;
            {var subQ0=sQuery(id+"F4.wireOp",EDGE,"E30");Q3=makeQuery(id+"F8.boolean.opBoolean","SPLIT",EDGE,{"disambiguationData":[TD([makeQuery(id+"F5.opExtrude","SWEPT_FACE",FACE,{"disambiguationData":[OSD([sQuery(id+"F4.wireOp",EDGE,"E35.filletArc")])]})])],"derivedFrom":makeQuery(id+"F5.opExtrude","CAP_EDGE",EDGE,{"disambiguationData":[OSD([subQ0])],"isStart":false})});}
            var Q4;
            {var subQ0=sQuery(id+"F0.wireOp",EDGE,"E25.7");var subQ1=sQuery(id+"F0.wireOp",EDGE,"E25.1");var subQ2=sQuery(id+"F0.wireOp",EDGE,"E25.6");var subQ3=sQuery(id+"F0.wireOp",EDGE,"E25.5");var subQ4=sQuery(id+"F0.wireOp",EDGE,"E25.4");var subQ5=sQuery(id+"F0.wireOp",EDGE,"E25.0");var subQ6=sQuery(id+"F0.wireOp",EDGE,"E25.2");var subQ7=sQuery(id+"F0.wireOp",EDGE,"E25.3");Q4=makeQuery(id+"F8.boolean.opBoolean","INTERSECT",EDGE,{"derivedFrom":[makeQuery(id+"F5.boolean.opBoolean","SPLIT",FACE,{"disambiguationData":[TD([makeQuery(id+"F2.opExtrude","SWEPT_FACE",FACE,{"disambiguationData":[OSD([subQ5])]})])],"derivedFrom":makeQuery(id+"F3.boolean.opBoolean","COPY",FACE,{"derivedFrom":makeQuery(id+"F3.opExtrude","CAP_FACE",FACE,{"disambiguationData":[OSD([subQ5,subQ1,subQ6,subQ7,subQ4,subQ3,subQ2,subQ0])],"isStart":false})})}),makeQuery(id+"F8.opExtrude","SWEPT_FACE",FACE,{"disambiguationData":[OSD([sQuery(id+"F7.wireOp",EDGE,"E67")])]})]});}
            var Q5;
            Q5=makeQuery(id+"F8.boolean.opBoolean","INTERSECT",EDGE,{"disambiguationData":[OD(0.0)],"derivedFrom":[makeQuery(id+"F5.opExtrude","SWEPT_FACE",FACE,{"disambiguationData":[OSD([sQuery(id+"F4.wireOp",EDGE,"E30")])]}),makeQuery(id+"F8.opExtrude","SWEPT_FACE",FACE,{"disambiguationData":[OSD([sQuery(id+"F7.wireOp",EDGE,"E67")])]})]});
            fillet(context, id + "F14", {"entities" : qUnion([Q0, Q1, Q2, Q3, Q4, Q5]), "radius" : 3 * mm, "tangentPropagation" : true, "allowEdgeOverflow" : false});
        }
        {
            var Q0;
            Q0=makeQuery(id+"F1.opExtrude","CAP_EDGE",EDGE,{"disambiguationData":[OSD([sQuery(id+"F0.wireOp",EDGE,"E1.bottom")])],"isStart":false});
            fillet(context, id + "F15", {"entities" : qUnion([Q0]), "radius" : 2 * mm, "tangentPropagation" : true, "allowEdgeOverflow" : false});
        }
        {
            var Q0;
            {var subQ0=sQuery(id+"F0.wireOp",EDGE,"E21.filletArc");var subQ1=sQuery(id+"F0.wireOp",EDGE,"E7");var subQ2=sQuery(id+"F0.wireOp",EDGE,"E6");var subQ3=sQuery(id+"F0.wireOp",EDGE,"E5");var subQ4=sQuery(id+"F0.wireOp",EDGE,"E4");var subQ5=sQuery(id+"F0.wireOp",EDGE,"E22.filletArc");var subQ6=sQuery(id+"F0.wireOp",EDGE,"E1.bottom");var subQ7=sQuery(id+"F0.wireOp",EDGE,"E1.right");var subQ8=sQuery(id+"F0.wireOp",EDGE,"E1.top");var subQ9=sQuery(id+"F0.wireOp",EDGE,"E1.left");var subQ10=sQuery(id+"F0.wireOp",EDGE,"E23.filletArc");var subQ11=sQuery(id+"F0.wireOp",EDGE,"E24.filletArc");Q0=makeQuery(id+"F2.boolean.opBoolean","SPLIT",FACE,{"disambiguationData":[TD([makeQuery(id+"F1.opExtrude","SWEPT_FACE",FACE,{"disambiguationData":[OSD([subQ6])]})])],"derivedFrom":makeQuery(id+"F1.opExtrude","CAP_FACE",FACE,{"disambiguationData":[OSD([subQ6,subQ8,subQ9,subQ7,subQ4,subQ3,subQ2,subQ1,subQ0,subQ5,subQ10,subQ11])],"isStart":true})});}
            var sketch = newSketch(context, id + "F16", { "sketchPlane" : qUnion([Q0])});
            skLineSegment(sketch, "E79.0", {"start": v(-70, 90) * mm, "end": v(70, 90) * mm});
            skArc(sketch, "E80.0", {"start": v(80, 80) * mm, "mid": v(77.07, 87.07) * mm, "end": v(70, 90) * mm});
            skLineSegment(sketch, "E81.0", {"start": v(80, -80) * mm, "end": v(80, 80) * mm});
            skLineSegment(sketch, "E82.0", {"start": v(-80, -80) * mm, "end": v(-80, 80) * mm});
            skArc(sketch, "E83.0", {"start": v(-70, 90) * mm, "mid": v(-77.07, 87.07) * mm, "end": v(-80, 80) * mm});
            skLineSegment(sketch, "E84.0", {"start": v(-70, -90) * mm, "end": v(70, -90) * mm});
            skArc(sketch, "E85.0", {"start": v(-80, -80) * mm, "mid": v(-77.07, -87.07) * mm, "end": v(-70, -90) * mm, "construction": true});
            skArc(sketch, "E86.0", {"start": v(70, -90) * mm, "mid": v(77.07, -87.07) * mm, "end": v(80, -80) * mm, "construction": true});
            skLineSegment(sketch, "E87", {"start": v(0, 90) * mm, "end": v(0, 120) * mm, "construction": true});
            skCircle(sketch, "E88", {"center": v(0, 120) * mm, "radius": 6 * mm});
            skLineSegment(sketch, "E89", {"start": v(-33.27, 90) * mm, "end": v(-15.27, 108) * mm});
            skLineSegment(sketch, "E90", {"start": v(-15.27, 108) * mm, "end": v(-15.27, 120) * mm});
            skLineSegment(sketch, "E91", {"start": v(32.73, 90) * mm, "end": v(14.73, 108) * mm});
            skLineSegment(sketch, "E92", {"start": v(14.73, 108) * mm, "end": v(14.73, 120) * mm});
            skArc(sketch, "E93", {"start": v(14.73, 120) * mm, "mid": v(-0.27, 135) * mm, "end": v(-15.27, 120) * mm});
            skLineSegment(sketch, "E94", {"start": v(-80, 0) * mm, "end": v(80, 0) * mm, "construction": true});
            skLineSegment(sketch, "E95.MirrorCS", {"start": v(32.73, -90) * mm, "end": v(14.73, -108) * mm});
            skLineSegment(sketch, "E96.MirrorCS", {"start": v(-33.27, -90) * mm, "end": v(-15.27, -108) * mm});
            skLineSegment(sketch, "E97.MirrorCS", {"start": v(14.73, -108) * mm, "end": v(14.73, -120) * mm});
            skLineSegment(sketch, "E98.MirrorCS", {"start": v(-15.27, -108) * mm, "end": v(-15.27, -120) * mm});
            skArc(sketch, "E99.MirrorCS", {"start": v(14.73, -120) * mm, "mid": v(-0.27, -135) * mm, "end": v(-15.27, -120) * mm});
            skCircle(sketch, "E100.MirrorC", {"center": v(0, -120) * mm, "radius": 6 * mm});
            skLineSegment(sketch, "E101.MirrorCS", {"start": v(0, -90) * mm, "end": v(0, -120) * mm, "construction": true});
            skSolve(sketch);
        }
        {
            var Q0;
            Q0=makeQuery(id+"F16.imprint","IMPRINT",FACE,{"disambiguationData":[TD([[makeQuery(id+"F16.imprint","IMPRINT",EDGE,{"derivedFrom":sQuery(id+"F16.wireOp",EDGE,"E88")}),-1.0]])]});
            var Q1;
            {var subQ1=sQuery(id+"F16.wireOp",EDGE,"E80.0");Q1=makeQuery(id+"F16.imprint","IMPRINT",FACE,{"disambiguationData":[TD([[makeQuery(id+"F16.imprint","IMPRINT",EDGE,{"derivedFrom":subQ1}),1.0]])]});}
            var Q2;
            {var subQ1=sQuery(id+"F16.wireOp",EDGE,"E95.MirrorCS");Q2=makeQuery(id+"F16.imprint","IMPRINT",FACE,{"disambiguationData":[TD([[makeQuery(id+"F16.imprint","IMPRINT",EDGE,{"derivedFrom":subQ1}),-1.0]])]});}
            var Q3;
            Q3=makeQuery(id+"F2.opExtrude","CAP_FACE",FACE,{"disambiguationData":[OSD([sQuery(id+"F0.wireOp",EDGE,"E12"),sQuery(id+"F0.wireOp",EDGE,"E13"),sQuery(id+"F0.wireOp",EDGE,"E14"),sQuery(id+"F0.wireOp",EDGE,"E15"),sQuery(id+"F0.wireOp",EDGE,"E17.filletArc"),sQuery(id+"F0.wireOp",EDGE,"E18.filletArc"),sQuery(id+"F0.wireOp",EDGE,"E19.filletArc"),sQuery(id+"F0.wireOp",EDGE,"E20.filletArc"),sQuery(id+"F0.wireOp",EDGE,"E25.0"),sQuery(id+"F0.wireOp",EDGE,"E25.1"),sQuery(id+"F0.wireOp",EDGE,"E25.2"),sQuery(id+"F0.wireOp",EDGE,"E25.3"),sQuery(id+"F0.wireOp",EDGE,"E25.4"),sQuery(id+"F0.wireOp",EDGE,"E25.5"),sQuery(id+"F0.wireOp",EDGE,"E25.6"),sQuery(id+"F0.wireOp",EDGE,"E25.7")])],"isStart":false});
            extrude(context, id + "F17", {"entities" : qUnion([Q0, Q1, Q2]), "endBound" : BoundingType.UP_TO_SURFACE, "endBoundEntityFace" : qUnion([Q3]), "depth" : 25 * mm});
        }
    });
